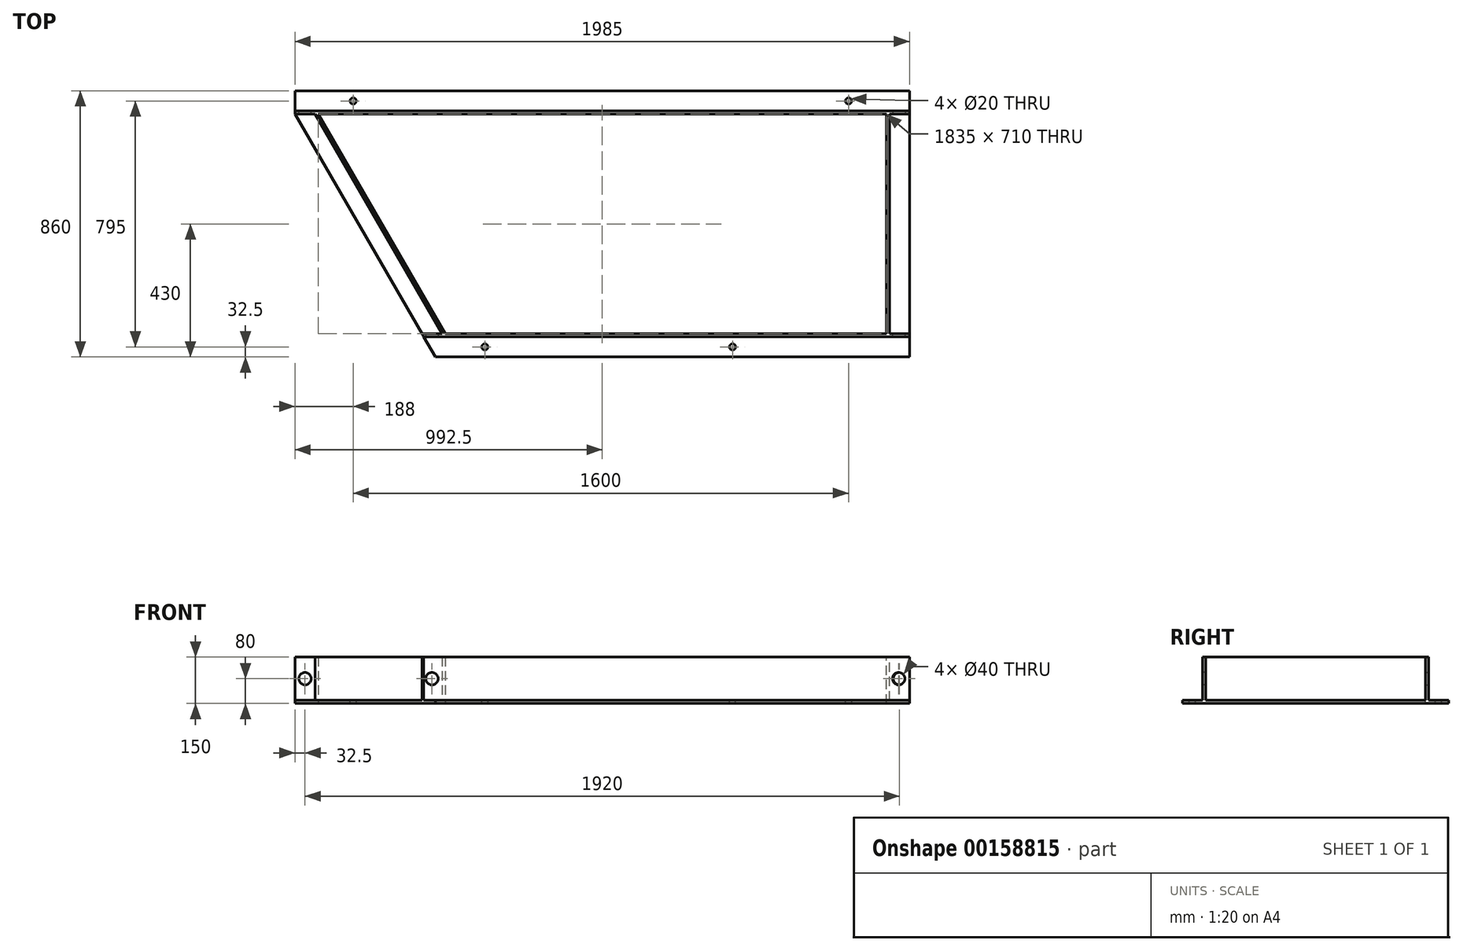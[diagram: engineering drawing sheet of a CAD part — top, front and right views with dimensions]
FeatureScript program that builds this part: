
annotation { "Feature Type Name" : "Feature", "Feature Type Description" : "" }
export const myFeature = defineFeature(function(context is Context, id is Id, definition is map)
    precondition{}
    {
        {
            var Q0;
            Q0=qCreatedBy(makeId("Right.planeOp"),FACE);
            var sketch = newSketch(context, id + "F0", { "sketchPlane" : qUnion([Q0])});
            skLineSegment(sketch, "E0.bottom", {"start": v(0, 0) * mm, "end": v(10, 0) * mm});
            skLineSegment(sketch, "E0.top", {"start": v(0, 150) * mm, "end": v(10, 150) * mm});
            skLineSegment(sketch, "E0.left", {"start": v(0, 0) * mm, "end": v(0, 150) * mm});
            skLineSegment(sketch, "E0.right", {"start": v(10, 10) * mm, "end": v(10, 150) * mm});
            skLineSegment(sketch, "E1.bottom", {"start": v(0, 0) * mm, "end": v(75, 0) * mm});
            skLineSegment(sketch, "E1.top", {"start": v(10, 10) * mm, "end": v(75, 10) * mm});
            skLineSegment(sketch, "E1.left", {"start": v(0, 0) * mm, "end": v(0, 10) * mm});
            skLineSegment(sketch, "E1.right", {"start": v(75, 0) * mm, "end": v(75, 10) * mm});
            skSolve(sketch);
        }
        {
            var Q0;
            Q0=qSketchRegion(id+"F0",true);
            extrude(context, id + "F1", {"entities" : qUnion([Q0]), "depth" : 1985 * mm});
        }
        {
            var Q0;
            Q0=makeQuery(id+"F1.opExtrude","SWEPT_FACE",FACE,{"disambiguationData":[OSD([sQuery(id+"F0.wireOp",EDGE,"E0.left"),sQuery(id+"F0.wireOp",EDGE,"E1.left")])]});
            var sketch = newSketch(context, id + "F2", { "sketchPlane" : qUnion([Q0])});
            skLineSegment(sketch, "E2.bottom", {"start": v(1910, 0) * mm, "end": v(1920, 0) * mm});
            skLineSegment(sketch, "E2.top", {"start": v(1910, 150) * mm, "end": v(1920, 150) * mm});
            skLineSegment(sketch, "E2.left", {"start": v(1910, 0) * mm, "end": v(1910, 150) * mm});
            skLineSegment(sketch, "E2.right", {"start": v(1920, 10) * mm, "end": v(1920, 150) * mm});
            skLineSegment(sketch, "E3.bottom", {"start": v(1910, 0) * mm, "end": v(1985, 0) * mm});
            skLineSegment(sketch, "E3.top", {"start": v(1920, 10) * mm, "end": v(1985, 10) * mm});
            skLineSegment(sketch, "E3.left", {"start": v(1910, 0) * mm, "end": v(1910, 10) * mm});
            skLineSegment(sketch, "E3.right", {"start": v(1985, 0) * mm, "end": v(1985, 10) * mm});
            skSolve(sketch);
        }
        {
            var Q0;
            Q0=qSketchRegion(id+"F2",true);
            extrude(context, id + "F3", {"entities" : qUnion([Q0]), "operationType" : NewBodyOperationType.ADD, "depth" : 710 * mm});
        }
        {
            var Q0;
            Q0=makeQuery(id+"F3.boolean.opBoolean","MERGE",FACE,{"derivedFrom":[makeQuery(id+"F1.opExtrude","CAP_FACE",FACE,{"disambiguationData":[OSD([sQuery(id+"F0.wireOp",EDGE,"E0.top"),sQuery(id+"F0.wireOp",EDGE,"E0.left"),sQuery(id+"F0.wireOp",EDGE,"E0.right"),sQuery(id+"F0.wireOp",EDGE,"E1.bottom"),sQuery(id+"F0.wireOp",EDGE,"E1.top"),sQuery(id+"F0.wireOp",EDGE,"E1.left"),sQuery(id+"F0.wireOp",EDGE,"E1.right")])],"isStart":false}),makeQuery(id+"F3.opExtrude","SWEPT_FACE",FACE,{"disambiguationData":[OSD([sQuery(id+"F2.wireOp",EDGE,"E3.right")])]})]});
            var sketch = newSketch(context, id + "F4", { "sketchPlane" : qUnion([Q0])});
            skLineSegment(sketch, "E4.bottom", {"start": v(-720, 10) * mm, "end": v(-785, 10) * mm});
            skLineSegment(sketch, "E4.top", {"start": v(-710, 0) * mm, "end": v(-785, 0) * mm});
            skLineSegment(sketch, "E4.left", {"start": v(-710, 10) * mm, "end": v(-710, 0) * mm});
            skLineSegment(sketch, "E4.right", {"start": v(-785, 10) * mm, "end": v(-785, 0) * mm});
            skLineSegment(sketch, "E5.bottom", {"start": v(-710, 0) * mm, "end": v(-720, 0) * mm});
            skLineSegment(sketch, "E5.top", {"start": v(-710, 150) * mm, "end": v(-720, 150) * mm});
            skLineSegment(sketch, "E5.left", {"start": v(-710, 0) * mm, "end": v(-710, 150) * mm});
            skLineSegment(sketch, "E5.right", {"start": v(-720, 10) * mm, "end": v(-720, 150) * mm});
            skSolve(sketch);
        }
        {
            var Q0;
            Q0=qSketchRegion(id+"F4",true);
            extrude(context, id + "F5", {"entities" : qUnion([Q0]), "oppositeDirection" : true, "depth" : 1575 * mm});
        }
        {
            var Q0;
            Q0=qCreatedBy(makeId("Top.planeOp"),FACE);
            var sketch = newSketch(context, id + "F6", { "sketchPlane" : qUnion([Q0])});
            skLineSegment(sketch, "E6", {"start": v(75, 0) * mm, "end": v(485, -710) * mm});
            skLineSegment(sketch, "E7", {"start": v(75, 0) * mm, "end": v(0, 0) * mm});
            skLineSegment(sketch, "E8", {"start": v(0, 0) * mm, "end": v(410, -710) * mm});
            skLineSegment(sketch, "E9", {"start": v(410, -710) * mm, "end": v(485, -710) * mm});
            skSolve(sketch);
        }
        {
            var Q0;
            Q0=qSketchRegion(id+"F6",true);
            extrude(context, id + "F7", {"entities" : qUnion([Q0]), "depth" : 10 * mm});
        }
        {
            var Q0;
            Q0=makeQuery(id+"F7.opExtrude","CAP_FACE",FACE,{"disambiguationData":[OSD([sQuery(id+"F6.wireOp",EDGE,"E6"),sQuery(id+"F6.wireOp",EDGE,"E7"),sQuery(id+"F6.wireOp",EDGE,"E8"),sQuery(id+"F6.wireOp",EDGE,"E9")])],"isStart":false});
            var sketch = newSketch(context, id + "F8", { "sketchPlane" : qUnion([Q0])});
            skLineSegment(sketch, "E10", {"start": v(75, 0) * mm, "end": v(485, -710) * mm});
            skLineSegment(sketch, "E11", {"start": v(485, -710) * mm, "end": v(475, -710) * mm});
            skLineSegment(sketch, "E12", {"start": v(475, -710) * mm, "end": v(65, 0) * mm});
            skLineSegment(sketch, "E13", {"start": v(65, 0) * mm, "end": v(75, 0) * mm});
            skSolve(sketch);
        }
        {
            var Q0;
            Q0=qSketchRegion(id+"F8",true);
            extrude(context, id + "F9", {"entities" : qUnion([Q0]), "operationType" : NewBodyOperationType.ADD, "depth" : 140 * mm});
        }
        {
            var Q0;
            Q0=makeQuery(id+"F5.opExtrude","SWEPT_FACE",FACE,{"disambiguationData":[OSD([sQuery(id+"F4.wireOp",EDGE,"E4.bottom")])]});
            var sketch = newSketch(context, id + "F10", { "sketchPlane" : qUnion([Q0])});
            skCircle(sketch, "E14", {"center": v(613.31, -752.5) * mm, "radius": 10 * mm});
            skCircle(sketch, "E15", {"center": v(1413.31, -752.5) * mm, "radius": 10 * mm});
            skCircle(sketch, "E16", {"center": v(1788, 42.5) * mm, "radius": 10 * mm});
            skCircle(sketch, "E17", {"center": v(188, 42.5) * mm, "radius": 10 * mm});
            skSolve(sketch);
        }
        {
            var Q0;
            Q0=qSketchRegion(id+"F10",true);
            extrude(context, id + "F11", {"entities" : qUnion([Q0]), "operationType" : NewBodyOperationType.REMOVE, "oppositeDirection" : true, "depth" : 25 * mm});
        }
        {
            var Q0;
            Q0=makeQuery(id+"F5.opExtrude","SWEPT_FACE",FACE,{"disambiguationData":[OSD([sQuery(id+"F4.wireOp",EDGE,"E5.right")])]});
            var sketch = newSketch(context, id + "F12", { "sketchPlane" : qUnion([Q0])});
            skCircle(sketch, "E18", {"center": v(442.5, 80) * mm, "radius": 20 * mm});
            skCircle(sketch, "E19", {"center": v(1950, 80) * mm, "radius": 20 * mm});
            skSolve(sketch);
        }
        {
            var Q0;
            Q0=qSketchRegion(id+"F12",true);
            extrude(context, id + "F13", {"entities" : qUnion([Q0]), "operationType" : NewBodyOperationType.REMOVE, "oppositeDirection" : true, "depth" : 15 * mm});
        }
        {
            var Q0;
            Q0=makeQuery(id+"F1.opExtrude","SWEPT_FACE",FACE,{"disambiguationData":[OSD([sQuery(id+"F0.wireOp",EDGE,"E0.right")])]});
            var sketch = newSketch(context, id + "F14", { "sketchPlane" : qUnion([Q0])});
            skCircle(sketch, "E20", {"center": v(-1952.5, 80) * mm, "radius": 20 * mm});
            skCircle(sketch, "E21", {"center": v(-32.5, 80) * mm, "radius": 20 * mm});
            skSolve(sketch);
        }
        {
            var Q0;
            Q0=qSketchRegion(id+"F14",true);
            extrude(context, id + "F15", {"entities" : qUnion([Q0]), "operationType" : NewBodyOperationType.REMOVE, "oppositeDirection" : true, "depth" : 25 * mm});
        }
        {
            var Q0;
            Q0=makeQuery(id+"F5.opExtrude","SWEPT_FACE",FACE,{"disambiguationData":[OSD([sQuery(id+"F4.wireOp",EDGE,"E4.bottom")])]});
            var sketch = newSketch(context, id + "F16", { "sketchPlane" : qUnion([Q0])});
            skLineSegment(sketch, "E22.0", {"start": v(0, 0) * mm, "end": v(410, -710) * mm});
            skLineSegment(sketch, "E23", {"start": v(410, -710) * mm, "end": v(453.3, -785) * mm});
            skLineSegment(sketch, "E24", {"start": v(453.3, -785) * mm, "end": v(410, -785) * mm});
            skLineSegment(sketch, "E25", {"start": v(410, -785) * mm, "end": v(410, -710) * mm});
            skSolve(sketch);
        }
        {
            var Q0;
            Q0=qSketchRegion(id+"F16",true);
            extrude(context, id + "F17", {"entities" : qUnion([Q0]), "operationType" : NewBodyOperationType.REMOVE, "depth" : 177 * mm, "hasSecondDirection" : true, "secondDirectionOppositeDirection" : true, "secondDirectionDepth" : 25 * mm});
        }
    });
